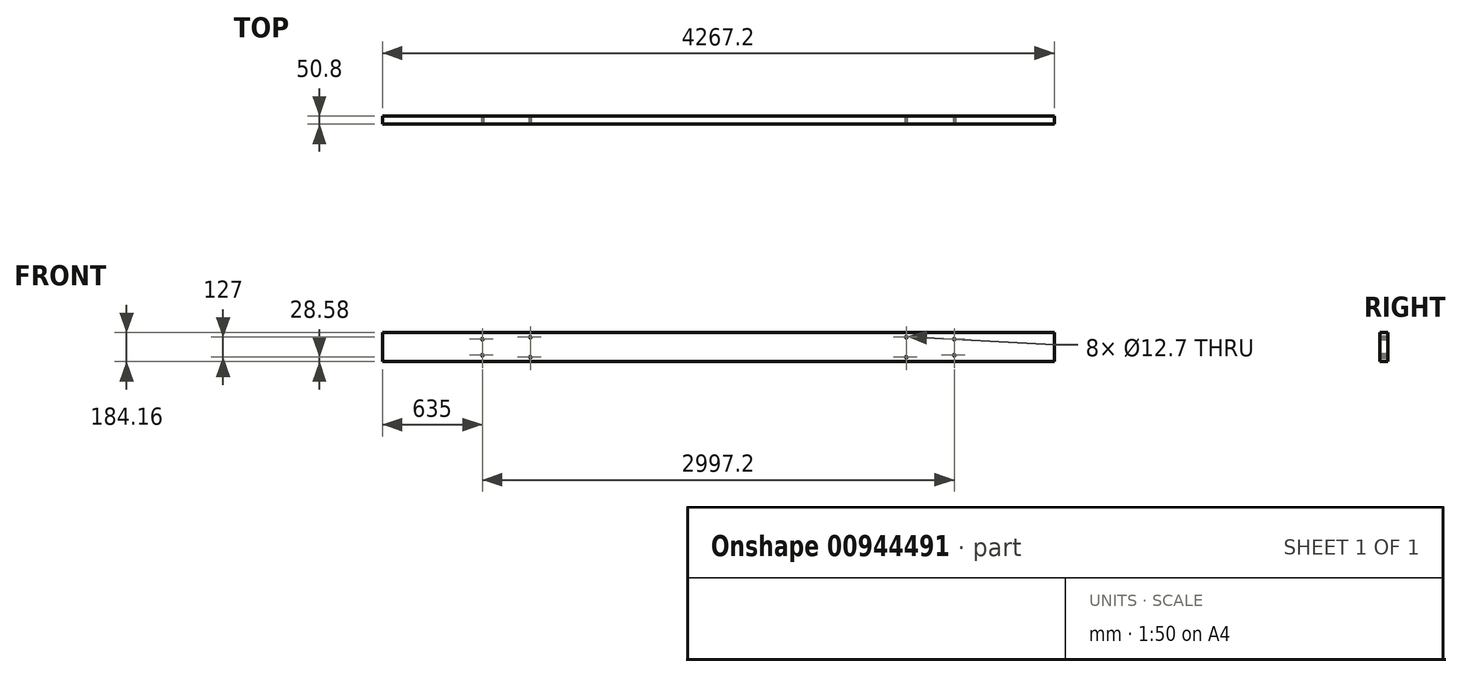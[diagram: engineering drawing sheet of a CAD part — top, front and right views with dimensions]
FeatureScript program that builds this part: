
annotation { "Feature Type Name" : "Feature", "Feature Type Description" : "" }
export const myFeature = defineFeature(function(context is Context, id is Id, definition is map)
    precondition{}
    {
        {
            var Q0;
            Q0=qCreatedBy(makeId("Front.planeOp"),FACE);
            var sketch = newSketch(context, id + "F0", { "sketchPlane" : qUnion([Q0])});
            skLineSegment(sketch, "E0.bottom", {"start": v(2133.6, -92.08) * mm, "end": v(-2133.6, -92.08) * mm});
            skLineSegment(sketch, "E0.top", {"start": v(2133.6, 92.08) * mm, "end": v(-2133.6, 92.07) * mm});
            skLineSegment(sketch, "E0.left", {"start": v(2133.6, -92.08) * mm, "end": v(2133.6, 92.08) * mm});
            skLineSegment(sketch, "E0.right", {"start": v(-2133.6, -92.08) * mm, "end": v(-2133.6, 92.07) * mm});
            skPoint(sketch, "E0.middle", {"position": v(0, 0) * mm});
            skSolve(sketch);
        }
        {
            var Q0;
            Q0=qSketchRegion(id+"F0",true);
            extrude(context, id + "F1", {"entities" : qUnion([Q0]), "depth" : 50.8 * mm, "offsetDistance" : 25.4 * mm});
        }
        {
            var Q0;
            Q0=makeQuery(id+"F1.opExtrude","CAP_FACE",FACE,{"disambiguationData":[OSD([sQuery(id+"F0.wireOp",EDGE,"E0.bottom"),sQuery(id+"F0.wireOp",EDGE,"E0.top"),sQuery(id+"F0.wireOp",EDGE,"E0.left"),sQuery(id+"F0.wireOp",EDGE,"E0.right")])],"isStart":false});
            var sketch = newSketch(context, id + "F2", { "sketchPlane" : qUnion([Q0])});
            skLineSegment(sketch, "E1.bottom", {"start": v(1498.6, -50.8) * mm, "end": v(-1498.6, -50.8) * mm, "construction": true});
            skLineSegment(sketch, "E1.top", {"start": v(1498.6, 50.8) * mm, "end": v(-1498.6, 50.8) * mm, "construction": true});
            skLineSegment(sketch, "E1.left", {"start": v(1498.6, -50.8) * mm, "end": v(1498.6, 50.8) * mm, "construction": true});
            skLineSegment(sketch, "E1.right", {"start": v(-1498.6, -50.8) * mm, "end": v(-1498.6, 50.8) * mm, "construction": true});
            skPoint(sketch, "E1.middle", {"position": v(0, 0) * mm});
            skCircle(sketch, "E2", {"center": v(1498.6, 50.8) * mm, "radius": 6.35 * mm});
            skCircle(sketch, "E3", {"center": v(1498.6, -50.8) * mm, "radius": 6.35 * mm});
            skCircle(sketch, "E4", {"center": v(-1498.6, 50.8) * mm, "radius": 6.35 * mm});
            skCircle(sketch, "E5", {"center": v(-1498.6, -50.8) * mm, "radius": 6.35 * mm});
            skSolve(sketch);
        }
        {
            var Q0;
            Q0=qSketchRegion(id+"F2",true);
            extrude(context, id + "F3", {"entities" : qUnion([Q0]), "operationType" : NewBodyOperationType.REMOVE, "oppositeDirection" : true, "depth" : 50.8 * mm, "offsetDistance" : 25.4 * mm});
        }
        {
            var Q0;
            Q0=qCreatedBy(makeId("Front.planeOp"),FACE);
            var sketch = newSketch(context, id + "F4", { "sketchPlane" : qUnion([Q0])});
            skLineSegment(sketch, "E6.bottom", {"start": v(1193.8, -63.5) * mm, "end": v(-1193.8, -63.5) * mm, "construction": true});
            skLineSegment(sketch, "E6.top", {"start": v(1193.8, 63.5) * mm, "end": v(-1193.8, 63.5) * mm, "construction": true});
            skLineSegment(sketch, "E6.left", {"start": v(1193.8, -63.5) * mm, "end": v(1193.8, 63.5) * mm, "construction": true});
            skLineSegment(sketch, "E6.right", {"start": v(-1193.8, -63.5) * mm, "end": v(-1193.8, 63.5) * mm, "construction": true});
            skPoint(sketch, "E6.middle", {"position": v(0, 0) * mm});
            skCircle(sketch, "E7", {"center": v(-1193.8, 63.5) * mm, "radius": 6.35 * mm});
            skCircle(sketch, "E8", {"center": v(-1193.8, -63.5) * mm, "radius": 6.35 * mm});
            skCircle(sketch, "E9", {"center": v(1193.8, 63.5) * mm, "radius": 6.35 * mm});
            skCircle(sketch, "E10", {"center": v(1193.8, -63.5) * mm, "radius": 6.35 * mm});
            skSolve(sketch);
        }
        {
            var Q0;
            Q0=qSketchRegion(id+"F4",true);
            extrude(context, id + "F5", {"entities" : qUnion([Q0]), "operationType" : NewBodyOperationType.REMOVE, "endBound" : BoundingType.SYMMETRIC, "depth" : 101.6 * mm, "offsetDistance" : 25.4 * mm});
        }
    });
